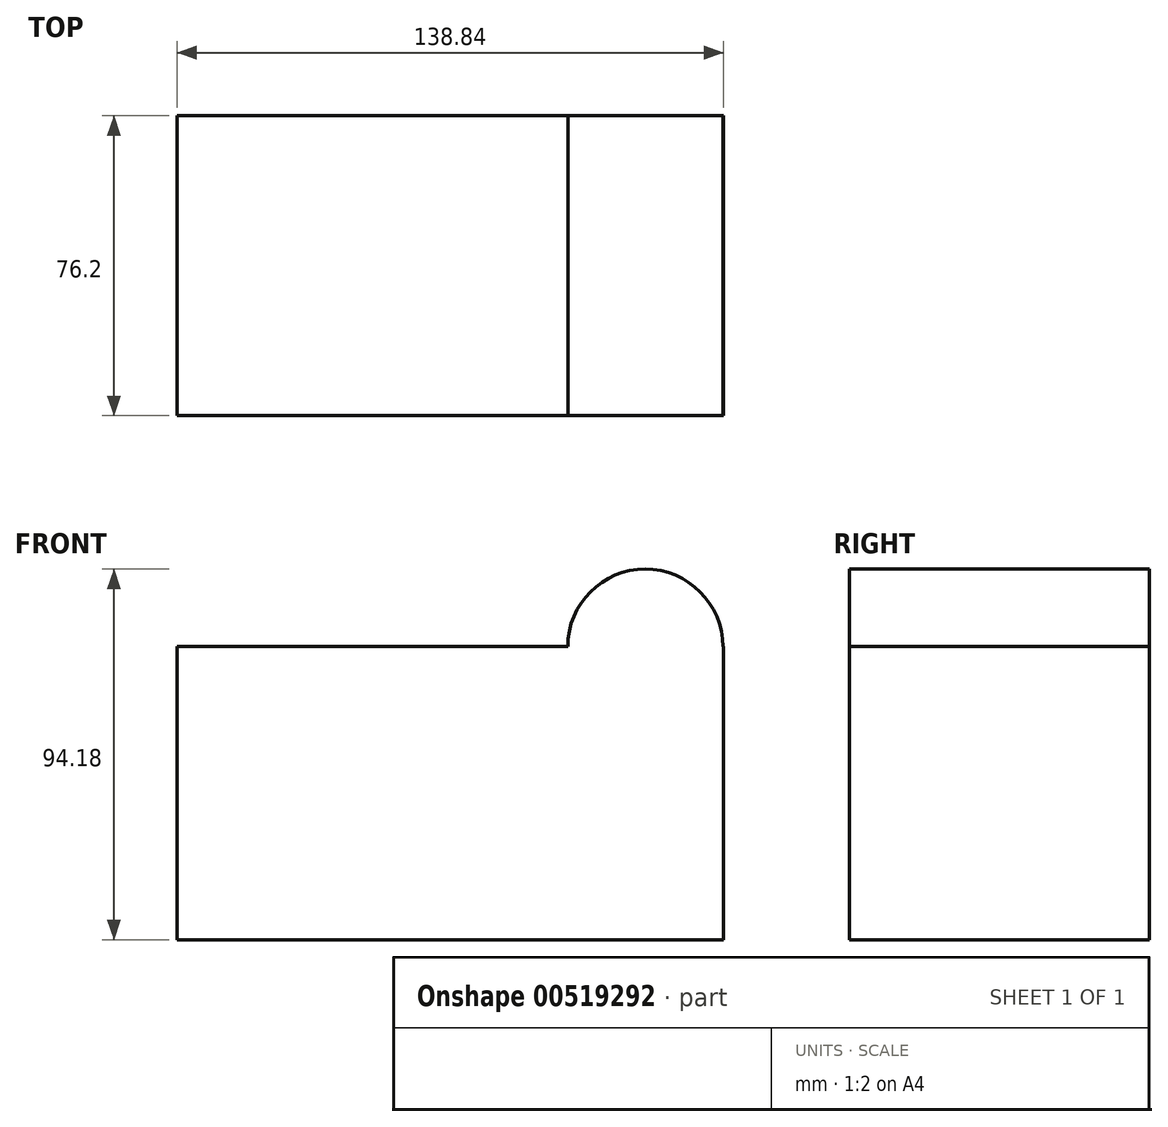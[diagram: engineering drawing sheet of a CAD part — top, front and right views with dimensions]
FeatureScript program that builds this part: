
annotation { "Feature Type Name" : "Feature", "Feature Type Description" : "" }
export const myFeature = defineFeature(function(context is Context, id is Id, definition is map)
    precondition{}
    {
        {
            var Q0;
            Q0=qCreatedBy(makeId("Front.planeOp"),FACE);
            var sketch = newSketch(context, id + "F0", { "sketchPlane" : qUnion([Q0])});
            skLineSegment(sketch, "E0.bottom", {"start": v(-19.84, 37.24) * mm, "end": v(-19.7, 37.24) * mm});
            skLineSegment(sketch, "E0.top", {"start": v(-19.84, -37.24) * mm, "end": v(19.84, -37.24) * mm});
            skLineSegment(sketch, "E0.left", {"start": v(-19.84, 37.24) * mm, "end": v(-19.84, -37.24) * mm});
            skLineSegment(sketch, "E0.right", {"start": v(19.84, 37.24) * mm, "end": v(19.84, -37.24) * mm});
            skPoint(sketch, "E0.middle", {"position": v(0, 0) * mm});
            skArc(sketch, "E1", {"start": v(19.7, 37.24) * mm, "mid": v(0, 56.94) * mm, "end": v(-19.7, 37.24) * mm});
            skCircle(sketch, "E2", {"center": v(0, 37.24) * mm, "radius": 8.55 * mm});
            skLineSegment(sketch, "E3.trimOffspring", {"start": v(19.7, 37.24) * mm, "end": v(19.84, 37.24) * mm});
            skSolve(sketch);
        }
        {
            var Q0;
            Q0=makeQuery(id+"F0.imprint","IMPRINT",FACE,{"disambiguationData":[TD([[makeQuery(id+"F0.imprint","IMPRINT",EDGE,{"derivedFrom":sQuery(id+"F0.wireOp",EDGE,"E0.bottom")}),-1.0]])]});
            var Q1;
            Q1=makeQuery(id+"F0.imprint","IMPRINT",FACE,{"disambiguationData":[TD([[makeQuery(id+"F0.imprint","IMPRINT",EDGE,{"derivedFrom":sQuery(id+"F0.wireOp",EDGE,"E2")}),1.0]])]});
            extrude(context, id + "F1", {"entities" : qUnion([Q0, Q1]), "depth" : 76.2 * mm, "offsetDistance" : 25.4 * mm});
        }
        {
            var Q0;
            Q0=makeQuery(id+"F1.opExtrude","SWEPT_FACE",FACE,{"disambiguationData":[OSD([sQuery(id+"F0.wireOp",EDGE,"E0.left")])]});
            extrude(context, id + "F2", {"entities" : qUnion([Q0]), "operationType" : NewBodyOperationType.ADD, "depth" : 99.16 * mm, "offsetDistance" : 25.4 * mm});
        }
    });
